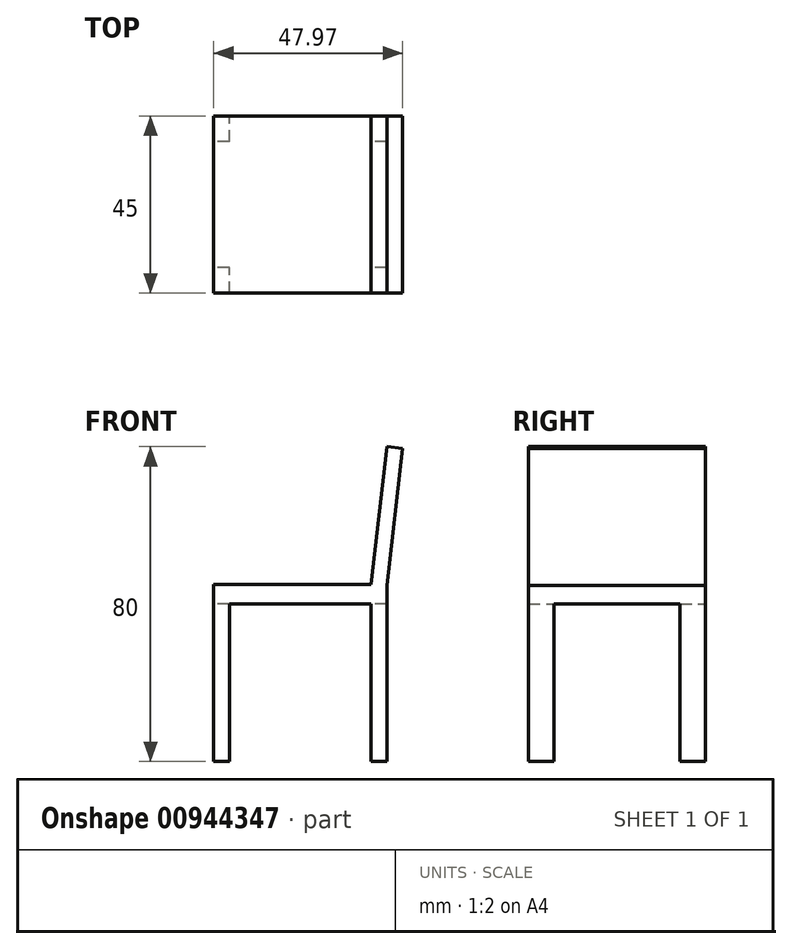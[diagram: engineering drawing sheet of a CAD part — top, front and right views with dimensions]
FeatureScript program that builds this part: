
annotation { "Feature Type Name" : "Feature", "Feature Type Description" : "" }
export const myFeature = defineFeature(function(context is Context, id is Id, definition is map)
    precondition{}
    {
        {
            var Q0;
            Q0=qCreatedBy(makeId("Front.planeOp"),FACE);
            var sketch = newSketch(context, id + "F0", { "sketchPlane" : qUnion([Q0])});
            skLineSegment(sketch, "E0", {"start": v(0, 0) * mm, "end": v(0, 44.77) * mm});
            skLineSegment(sketch, "E1", {"start": v(0, 44.77) * mm, "end": v(3.97, 79.55) * mm});
            skLineSegment(sketch, "E2", {"start": v(3.97, 79.55) * mm, "end": v(0, 80) * mm});
            skLineSegment(sketch, "E3", {"start": v(0, 80) * mm, "end": v(-4, 45) * mm});
            skLineSegment(sketch, "E4", {"start": v(-4, 45) * mm, "end": v(-44, 45) * mm});
            skLineSegment(sketch, "E5", {"start": v(-44, 45) * mm, "end": v(-44, 0) * mm});
            skLineSegment(sketch, "E6", {"start": v(-44, 0) * mm, "end": v(-40, 0) * mm});
            skLineSegment(sketch, "E7", {"start": v(-40, 0) * mm, "end": v(-40, 40) * mm});
            skLineSegment(sketch, "E8", {"start": v(-40, 40) * mm, "end": v(-4, 40) * mm});
            skLineSegment(sketch, "E9", {"start": v(-4, 40) * mm, "end": v(-4, 0) * mm});
            skLineSegment(sketch, "E10", {"start": v(-4, 0) * mm, "end": v(0, 0) * mm});
            skSolve(sketch);
        }
        {
            var Q0;
            Q0 = qSketchRegion(id + "F0", true);
            extrude(context, id + "F1", {"entities" : qUnion([Q0]), "depth" : 45 * mm, "offsetDistance" : 25 * mm});
        }
        {
            var Q0;
            Q0=makeQuery(id+"F1.opExtrude","SWEPT_FACE",FACE,{"disambiguationData":[OSD([sQuery(id+"F0.wireOp",EDGE,"E9")])]});
            var sketch = newSketch(context, id + "F2", { "sketchPlane" : qUnion([Q0])});
            skLineSegment(sketch, "E11", {"start": v(22.5, 0) * mm, "end": v(22.5, 40) * mm, "construction": true});
            skLineSegment(sketch, "E12.bottom", {"start": v(38.5, 0) * mm, "end": v(6.5, 0) * mm});
            skLineSegment(sketch, "E12.top", {"start": v(38.5, 40) * mm, "end": v(6.5, 40) * mm});
            skLineSegment(sketch, "E12.left", {"start": v(38.5, 0) * mm, "end": v(38.5, 40) * mm});
            skLineSegment(sketch, "E12.right", {"start": v(6.5, 0) * mm, "end": v(6.5, 40) * mm});
            skPoint(sketch, "E12.middle", {"position": v(22.5, 20) * mm});
            skSolve(sketch);
        }
        {
            var Q0;
            Q0 = qSketchRegion(id + "F2", true);
            extrude(context, id + "F3", {"entities" : qUnion([Q0]), "operationType" : NewBodyOperationType.REMOVE, "endBound" : BoundingType.THROUGH_ALL, "oppositeDirection" : true, "depth" : 25 * mm, "offsetDistance" : 25 * mm, "hasSecondDirection" : true, "secondDirectionBound" : BoundingType.THROUGH_ALL, "secondDirectionOppositeDirection" : false, "secondDirectionDepth" : 25 * mm});
        }
    });
